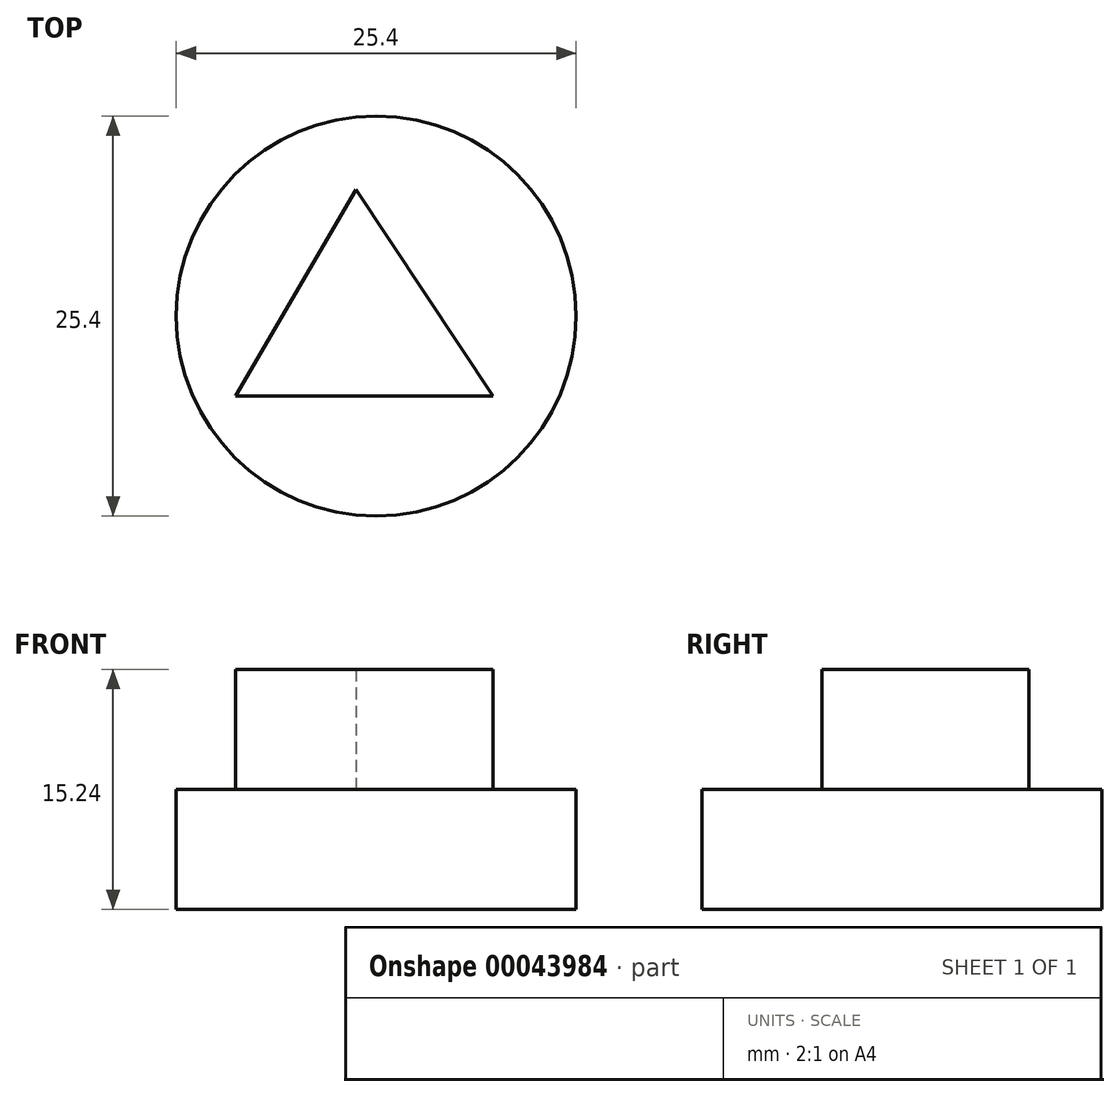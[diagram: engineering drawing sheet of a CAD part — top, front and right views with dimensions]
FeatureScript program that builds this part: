
annotation { "Feature Type Name" : "Feature", "Feature Type Description" : "" }
export const myFeature = defineFeature(function(context is Context, id is Id, definition is map)
    precondition{}
    {
        {
            var Q0;
            Q0=qCreatedBy(makeId("Top.planeOp"),FACE);
            var sketch = newSketch(context, id + "F0", { "sketchPlane" : qUnion([Q0])});
            skCircle(sketch, "E0", {"center": v(0, 0) * mm, "radius": 12.7 * mm});
            skSolve(sketch);
        }
        {
            var Q0;
            Q0=makeQuery(id+"F0.imprint","IMPRINT",FACE,{"disambiguationData":[TD([[makeQuery(id+"F0.imprint","IMPRINT",EDGE,{"derivedFrom":sQuery(id+"F0.wireOp",EDGE,"E0")}),1.0]])]});
            extrude(context, id + "F1", {"entities" : qUnion([Q0]), "depth" : 7.62 * mm});
        }
        {
            var Q0;
            Q0=makeQuery(id+"F1.opExtrude","CAP_FACE",FACE,{"disambiguationData":[OSD([sQuery(id+"F0.wireOp",EDGE,"E0")])],"isStart":false});
            var sketch = newSketch(context, id + "F2", { "sketchPlane" : qUnion([Q0])});
            skLineSegment(sketch, "E1", {"start": v(-1.27, 8.04) * mm, "end": v(-8.93, -5.1) * mm});
            skLineSegment(sketch, "E2", {"start": v(-8.93, -5.1) * mm, "end": v(7.41, -5.1) * mm});
            skLineSegment(sketch, "E3", {"start": v(7.41, -5.1) * mm, "end": v(-1.27, 8.04) * mm});
            skSolve(sketch);
        }
        {
            var Q0;
            Q0 = qSketchRegion(id + "F2", true);
            extrude(context, id + "F3", {"entities" : qUnion([Q0]), "depth" : 7.62 * mm});
        }
    });
